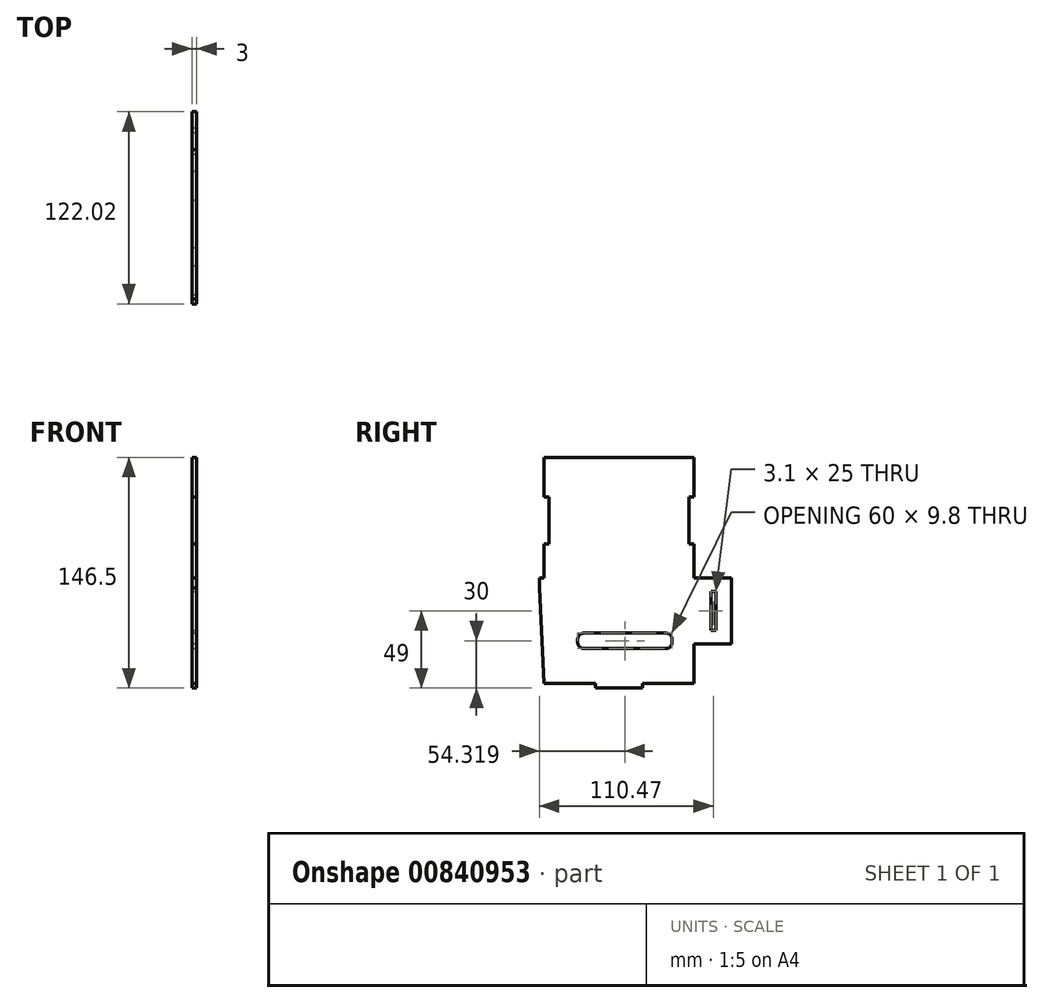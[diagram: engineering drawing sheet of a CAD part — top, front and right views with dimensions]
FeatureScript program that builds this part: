
annotation { "Feature Type Name" : "Feature", "Feature Type Description" : "" }
export const myFeature = defineFeature(function(context is Context, id is Id, definition is map)
    precondition{}
    {
        {
            var Q0;
            Q0=qCreatedBy(makeId("Right.planeOp"),FACE);
            var sketch = newSketch(context, id + "F0", { "sketchPlane" : qUnion([Q0])});
            skLineSegment(sketch, "E0", {"start": v(-45.8, 6.5) * mm, "end": v(-45.8, 83) * mm});
            skLineSegment(sketch, "E1", {"start": v(-45.8, 83) * mm, "end": v(49.2, 83) * mm});
            skLineSegment(sketch, "E2", {"start": v(49.2, 83) * mm, "end": v(49.2, 6.5) * mm});
            skLineSegment(sketch, "E3", {"start": v(49.2, 6.5) * mm, "end": v(73.2, 6.5) * mm});
            skLineSegment(sketch, "E4", {"start": v(73.2, 6.5) * mm, "end": v(73.2, -35.5) * mm});
            skLineSegment(sketch, "E5", {"start": v(73.2, -35.5) * mm, "end": v(49.2, -35.5) * mm});
            skLineSegment(sketch, "E6", {"start": v(49.2, -35.5) * mm, "end": v(49.2, -60.5) * mm});
            skLineSegment(sketch, "E7", {"start": v(-45.8, -60.5) * mm, "end": v(49.2, -60.5) * mm});
            skLineSegment(sketch, "E8", {"start": v(-45.8, 6.5) * mm, "end": v(-48.82, 6.5) * mm});
            skLineSegment(sketch, "E9", {"start": v(-48.82, 0) * mm, "end": v(-48.82, 6.5) * mm});
            skLineSegment(sketch, "E10", {"start": v(-48.82, 0) * mm, "end": v(-45.8, -60.5) * mm});
            skLineSegment(sketch, "E11", {"start": v(1.7, -60.5) * mm, "end": v(1.7, 83) * mm, "construction": true});
            skLineSegment(sketch, "E12.bottom", {"start": v(-13.3, -60.5) * mm, "end": v(16.7, -60.5) * mm});
            skLineSegment(sketch, "E12.top", {"start": v(-13.3, -63.5) * mm, "end": v(16.7, -63.5) * mm});
            skLineSegment(sketch, "E12.left", {"start": v(-13.3, -60.5) * mm, "end": v(-13.3, -63.5) * mm});
            skLineSegment(sketch, "E12.right", {"start": v(16.7, -60.5) * mm, "end": v(16.7, -63.5) * mm});
            skSolve(sketch);
        }
        {
            var Q0;
            Q0 = qSketchRegion(id + "F0", true);
            extrude(context, id + "F1", {"entities" : qUnion([Q0]), "depth" : 3 * mm, "offsetDistance" : 25 * mm});
        }
        {
            var Q0;
            Q0=makeQuery(id+"F1.opExtrude","CAP_FACE",FACE,{"disambiguationData":[OSD([sQuery(id+"F0.wireOp",EDGE,"949f8f8f-8a10-4c52-8d53-bf1458e5bfc2"),sQuery(id+"F0.wireOp",EDGE,"804f95c2-854d-4774-a781-587f4f921fa3"),sQuery(id+"F0.wireOp",EDGE,"E0"),sQuery(id+"F0.wireOp",EDGE,"E1"),sQuery(id+"F0.wireOp",EDGE,"E2"),sQuery(id+"F0.wireOp",EDGE,"E3"),sQuery(id+"F0.wireOp",EDGE,"E4"),sQuery(id+"F0.wireOp",EDGE,"E5"),sQuery(id+"F0.wireOp",EDGE,"E6"),sQuery(id+"F0.wireOp",EDGE,"daf7daeb-8f13-4c3d-9e17-d7c554ce6fb4")])],"isStart":false});
            var sketch = newSketch(context, id + "F2", { "sketchPlane" : qUnion([Q0])});
            skLineSegment(sketch, "E13.bottom", {"start": v(60.1, -2) * mm, "end": v(63.2, -2) * mm});
            skLineSegment(sketch, "E13.top", {"start": v(60.1, -27) * mm, "end": v(63.2, -27) * mm});
            skLineSegment(sketch, "E13.left", {"start": v(60.1, -2) * mm, "end": v(60.1, -27) * mm});
            skLineSegment(sketch, "E13.right", {"start": v(63.2, -2) * mm, "end": v(63.2, -27) * mm});
            skSolve(sketch);
        }
        {
            var Q0;
            Q0 = qSketchRegion(id + "F2", true);
            extrude(context, id + "F3", {"entities" : qUnion([Q0]), "operationType" : NewBodyOperationType.REMOVE, "oppositeDirection" : true, "depth" : 25 * mm, "offsetDistance" : 25 * mm});
        }
        {
            var Q0;
            Q0=makeQuery(id+"F1.opExtrude","CAP_FACE",FACE,{"disambiguationData":[OSD([sQuery(id+"F0.wireOp",EDGE,"E0"),sQuery(id+"F0.wireOp",EDGE,"E1"),sQuery(id+"F0.wireOp",EDGE,"E2"),sQuery(id+"F0.wireOp",EDGE,"E3"),sQuery(id+"F0.wireOp",EDGE,"E4"),sQuery(id+"F0.wireOp",EDGE,"E5"),sQuery(id+"F0.wireOp",EDGE,"E6"),sQuery(id+"F0.wireOp",EDGE,"HLK3Bjhx-9z3b-2Xyt-6boT-GLIaTX0Sabma"),sQuery(id+"F0.wireOp",EDGE,"E7")])],"isStart":false});
            var sketch = newSketch(context, id + "F4", { "sketchPlane" : qUnion([Q0])});
            skLineSegment(sketch, "E14.bottom", {"start": v(-20.5, -28.6) * mm, "end": v(31.5, -28.6) * mm});
            skLineSegment(sketch, "E14.top", {"start": v(-20.5, -38.4) * mm, "end": v(31.5, -38.4) * mm});
            skLineSegment(sketch, "E14.left", {"start": v(-24.5, -32.6) * mm, "end": v(-24.5, -34.4) * mm});
            skLineSegment(sketch, "E14.right", {"start": v(35.5, -32.6) * mm, "end": v(35.5, -34.4) * mm});
            skPoint(sketch, "E15.visualSharp", {"position": v(-24.5, -28.6) * mm});
            skArc(sketch, "E15.filletArc", {"start": v(-20.5, -28.6) * mm, "mid": v(-23.33, -29.77) * mm, "end": v(-24.5, -32.6) * mm});
            skPoint(sketch, "E16.visualSharp", {"position": v(-24.5, -38.4) * mm});
            skArc(sketch, "E16.filletArc", {"start": v(-24.5, -34.4) * mm, "mid": v(-23.33, -37.23) * mm, "end": v(-20.5, -38.4) * mm});
            skPoint(sketch, "E17.visualSharp", {"position": v(35.5, -28.6) * mm});
            skArc(sketch, "E17.filletArc", {"start": v(35.5, -32.6) * mm, "mid": v(34.33, -29.77) * mm, "end": v(31.5, -28.6) * mm});
            skPoint(sketch, "E18.visualSharp", {"position": v(35.5, -38.4) * mm});
            skArc(sketch, "E18.filletArc", {"start": v(31.5, -38.4) * mm, "mid": v(34.33, -37.23) * mm, "end": v(35.5, -34.4) * mm});
            skSolve(sketch);
        }
        {
            var Q0;
            Q0 = qSketchRegion(id + "F4", true);
            extrude(context, id + "F5", {"entities" : qUnion([Q0]), "operationType" : NewBodyOperationType.REMOVE, "oppositeDirection" : true, "depth" : 25 * mm, "offsetDistance" : 25 * mm});
        }
        {
            var Q0;
            Q0=makeQuery(id+"F1.opExtrude","CAP_FACE",FACE,{"disambiguationData":[OSD([sQuery(id+"F0.wireOp",EDGE,"E0"),sQuery(id+"F0.wireOp",EDGE,"E1"),sQuery(id+"F0.wireOp",EDGE,"E2"),sQuery(id+"F0.wireOp",EDGE,"E3"),sQuery(id+"F0.wireOp",EDGE,"E4"),sQuery(id+"F0.wireOp",EDGE,"E5"),sQuery(id+"F0.wireOp",EDGE,"E6"),sQuery(id+"F0.wireOp",EDGE,"E7"),sQuery(id+"F0.wireOp",EDGE,"E8"),sQuery(id+"F0.wireOp",EDGE,"E9"),sQuery(id+"F0.wireOp",EDGE,"E10"),sQuery(id+"F0.wireOp",EDGE,"E12.top"),sQuery(id+"F0.wireOp",EDGE,"E12.left"),sQuery(id+"F0.wireOp",EDGE,"E12.right")])],"isStart":false});
            var sketch = newSketch(context, id + "F6", { "sketchPlane" : qUnion([Q0])});
            skLineSegment(sketch, "E19.bottom", {"start": v(-45.8, 58) * mm, "end": v(-42.8, 58) * mm});
            skLineSegment(sketch, "E19.top", {"start": v(-45.8, 28) * mm, "end": v(-42.8, 28) * mm});
            skLineSegment(sketch, "E19.left", {"start": v(-45.8, 58) * mm, "end": v(-45.8, 28) * mm});
            skLineSegment(sketch, "E19.right", {"start": v(-42.8, 58) * mm, "end": v(-42.8, 28) * mm});
            skLineSegment(sketch, "E20", {"start": v(1.7, 83) * mm, "end": v(1.7, 47.27) * mm, "construction": true});
            skLineSegment(sketch, "E21.MirrorCS", {"start": v(49.2, 28) * mm, "end": v(46.2, 28) * mm});
            skLineSegment(sketch, "E22.MirrorCS", {"start": v(49.2, 58) * mm, "end": v(46.2, 58) * mm});
            skLineSegment(sketch, "E23.MirrorCS", {"start": v(49.2, 58) * mm, "end": v(49.2, 28) * mm});
            skLineSegment(sketch, "E24.MirrorCS", {"start": v(46.2, 58) * mm, "end": v(46.2, 28) * mm});
            skSolve(sketch);
        }
        {
            var Q0;
            Q0 = qSketchRegion(id + "F6", true);
            extrude(context, id + "F7", {"entities" : qUnion([Q0]), "operationType" : NewBodyOperationType.REMOVE, "oppositeDirection" : true, "depth" : 25 * mm, "offsetDistance" : 25 * mm});
        }
    });
